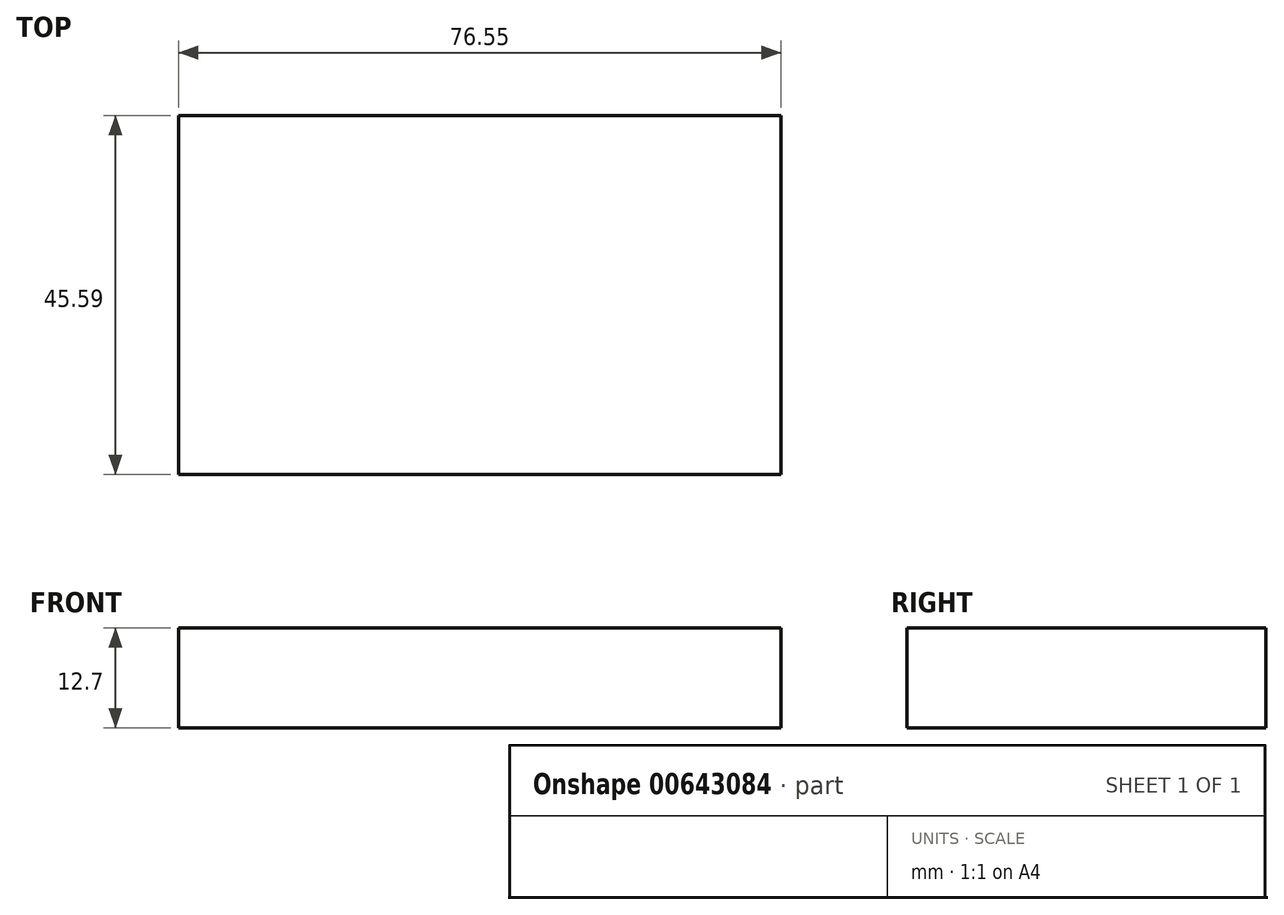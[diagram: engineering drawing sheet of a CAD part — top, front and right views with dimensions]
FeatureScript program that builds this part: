
annotation { "Feature Type Name" : "Feature", "Feature Type Description" : "" }
export const myFeature = defineFeature(function(context is Context, id is Id, definition is map)
    precondition{}
    {
        {
            var Q0;
            Q0=qCreatedBy(makeId("Top.planeOp"),FACE);
            var sketch = newSketch(context, id + "F0", { "sketchPlane" : qUnion([Q0])});
            skLineSegment(sketch, "E0.bottom", {"start": v(-76.55, 45.59) * mm, "end": v(0, 45.59) * mm});
            skLineSegment(sketch, "E0.top", {"start": v(-76.55, 0) * mm, "end": v(0, 0) * mm});
            skLineSegment(sketch, "E0.left", {"start": v(-76.55, 45.59) * mm, "end": v(-76.55, 0) * mm});
            skLineSegment(sketch, "E0.right", {"start": v(0, 45.59) * mm, "end": v(0, 0) * mm});
            skSolve(sketch);
        }
        {
            var Q0;
            Q0=makeQuery(id+"F0.imprint","IMPRINT",FACE,{"disambiguationData":[TD([[makeQuery(id+"F0.imprint","IMPRINT",EDGE,{"derivedFrom":sQuery(id+"F0.wireOp",EDGE,"E0.bottom")}),-1.0]])]});
            extrude(context, id + "F1", {"entities" : qUnion([Q0]), "depth" : 12.7 * mm, "offsetDistance" : 25.4 * mm});
        }
    });
